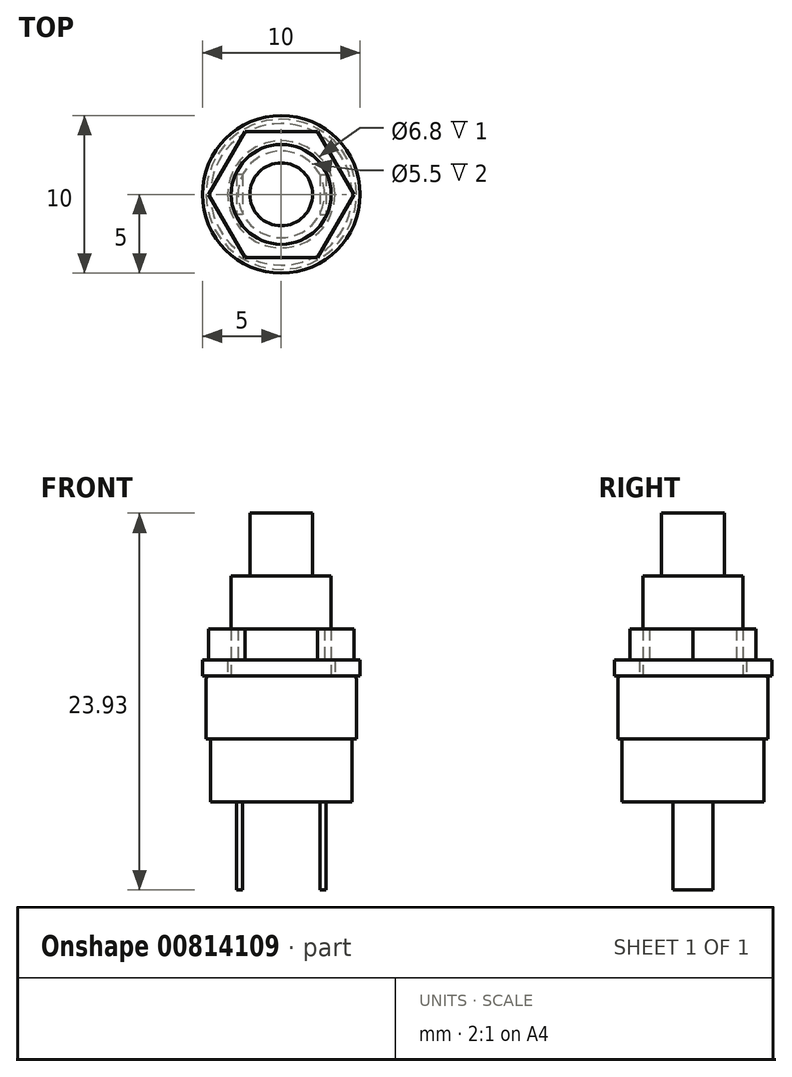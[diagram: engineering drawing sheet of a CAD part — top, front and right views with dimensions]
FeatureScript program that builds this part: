
annotation { "Feature Type Name" : "Feature", "Feature Type Description" : "" }
export const myFeature = defineFeature(function(context is Context, id is Id, definition is map)
    precondition{}
    {
        {
            var Q0;
            Q0=qCreatedBy(makeId("Top.planeOp"),FACE);
            var sketch = newSketch(context, id + "F0", { "sketchPlane" : qUnion([Q0])});
            skCircle(sketch, "E0", {"center": v(0, 0) * mm, "radius": 4.77 * mm});
            skCircle(sketch, "E1", {"center": v(0, 0) * mm, "radius": 4.5 * mm});
            skCircle(sketch, "E2", {"center": v(0, 0) * mm, "radius": 3.18 * mm});
            skCircle(sketch, "E3", {"center": v(0, 0) * mm, "radius": 2 * mm});
            skSolve(sketch);
        }
        {
            var Q0;
            Q0=makeQuery(id+"F0.imprint","IMPRINT",FACE,{"disambiguationData":[TD([[makeQuery(id+"F0.imprint","IMPRINT",EDGE,{"derivedFrom":sQuery(id+"F0.wireOp",EDGE,"E3")}),1.0]])]});
            extrude(context, id + "F1", {"entities" : qUnion([Q0]), "depth" : (10.35 + 4) * mm, "offsetDistance" : 25 * mm});
        }
        {
            var Q0;
            Q0=makeQuery(id+"F0.imprint","IMPRINT",FACE,{"disambiguationData":[TD([[makeQuery(id+"F0.imprint","IMPRINT",EDGE,{"derivedFrom":sQuery(id+"F0.wireOp",EDGE,"E3")}),1.0]])]});
            var Q1;
            Q1=makeQuery(id+"F0.imprint","IMPRINT",FACE,{"disambiguationData":[TD([[makeQuery(id+"F0.imprint","IMPRINT",EDGE,{"derivedFrom":sQuery(id+"F0.wireOp",EDGE,"E2")}),1.0]])]});
            extrude(context, id + "F2", {"entities" : qUnion([Q0, Q1]), "depth" : 10.35 * mm, "offsetDistance" : 25 * mm});
        }
        {
            var Q0;
            Q0=makeQuery(id+"F0.imprint","IMPRINT",FACE,{"disambiguationData":[TD([[makeQuery(id+"F0.imprint","IMPRINT",EDGE,{"derivedFrom":sQuery(id+"F0.wireOp",EDGE,"E0")}),1.0]])]});
            var Q1;
            Q1=makeQuery(id+"F0.imprint","IMPRINT",FACE,{"disambiguationData":[TD([[makeQuery(id+"F0.imprint","IMPRINT",EDGE,{"derivedFrom":sQuery(id+"F0.wireOp",EDGE,"E1")}),1.0]])]});
            var Q2;
            Q2=makeQuery(id+"F0.imprint","IMPRINT",FACE,{"disambiguationData":[TD([[makeQuery(id+"F0.imprint","IMPRINT",EDGE,{"derivedFrom":sQuery(id+"F0.wireOp",EDGE,"E2")}),1.0]])]});
            var Q3;
            Q3=makeQuery(id+"F0.imprint","IMPRINT",FACE,{"disambiguationData":[TD([[makeQuery(id+"F0.imprint","IMPRINT",EDGE,{"derivedFrom":sQuery(id+"F0.wireOp",EDGE,"E3")}),1.0]])]});
            extrude(context, id + "F3", {"entities" : qUnion([Q0, Q1, Q2, Q3]), "operationType" : NewBodyOperationType.ADD, "depth" : 4 * mm, "offsetDistance" : 25 * mm});
        }
        {
            var Q0;
            Q0=makeQuery(id+"F0.imprint","IMPRINT",FACE,{"disambiguationData":[TD([[makeQuery(id+"F0.imprint","IMPRINT",EDGE,{"derivedFrom":sQuery(id+"F0.wireOp",EDGE,"E3")}),1.0]])]});
            var Q1;
            Q1=makeQuery(id+"F0.imprint","IMPRINT",FACE,{"disambiguationData":[TD([[makeQuery(id+"F0.imprint","IMPRINT",EDGE,{"derivedFrom":sQuery(id+"F0.wireOp",EDGE,"E2")}),1.0]])]});
            var Q2;
            Q2=makeQuery(id+"F0.imprint","IMPRINT",FACE,{"disambiguationData":[TD([[makeQuery(id+"F0.imprint","IMPRINT",EDGE,{"derivedFrom":sQuery(id+"F0.wireOp",EDGE,"E1")}),1.0]])]});
            extrude(context, id + "F4", {"entities" : qUnion([Q0, Q1, Q2]), "operationType" : NewBodyOperationType.ADD, "oppositeDirection" : true, "depth" : 4 * mm, "offsetDistance" : 25 * mm});
        }
        {
            var Q0;
            Q0=makeQuery(id+"F4.opExtrude","CAP_FACE",FACE,{"disambiguationData":[OSD([sQuery(id+"F0.wireOp",EDGE,"E1")])],"isStart":false});
            var sketch = newSketch(context, id + "F5", { "sketchPlane" : qUnion([Q0])});
            skLineSegment(sketch, "E4", {"start": v(0, 5.46) * mm, "end": v(0, -5.9) * mm, "construction": true});
            skLineSegment(sketch, "E5", {"start": v(6.94, 0) * mm, "end": v(-5.97, 0) * mm, "construction": true});
            skLineSegment(sketch, "E6.bottom", {"start": v(-2.47, -1.27) * mm, "end": v(-2.85, -1.27) * mm});
            skLineSegment(sketch, "E6.top", {"start": v(-2.47, 1.27) * mm, "end": v(-2.85, 1.27) * mm});
            skLineSegment(sketch, "E6.left", {"start": v(-2.47, -1.27) * mm, "end": v(-2.47, 1.27) * mm});
            skLineSegment(sketch, "E6.right", {"start": v(-2.85, -1.27) * mm, "end": v(-2.85, 1.27) * mm});
            skPoint(sketch, "E6.middle", {"position": v(-2.65, 0) * mm});
            skLineSegment(sketch, "E7.MirrorCS", {"start": v(2.47, -1.27) * mm, "end": v(2.85, -1.27) * mm});
            skLineSegment(sketch, "E8.MirrorCS", {"start": v(2.47, 1.27) * mm, "end": v(2.85, 1.27) * mm});
            skPoint(sketch, "E9.MirrorP", {"position": v(2.65, 0) * mm});
            skLineSegment(sketch, "E10.MirrorCS", {"start": v(2.85, -1.27) * mm, "end": v(2.85, 1.27) * mm});
            skLineSegment(sketch, "E11.MirrorCS", {"start": v(2.47, -1.27) * mm, "end": v(2.47, 1.27) * mm});
            skSolve(sketch);
        }
        {
            var Q0;
            Q0 = qSketchRegion(id + "F5", true);
            extrude(context, id + "F6", {"entities" : qUnion([Q0]), "operationType" : NewBodyOperationType.ADD, "depth" : 5.6 * mm, "offsetDistance" : 25 * mm});
        }
        {
            var Q0;
            Q0=makeQuery(id+"F3.opExtrude","CAP_EDGE",EDGE,{"disambiguationData":[OSD([sQuery(id+"F0.wireOp",EDGE,"E0")])],"isStart":false});
            fillet(context, id + "F7", {"entities" : qUnion([Q0]), "radius" : 0.2 * mm, "tangentPropagation" : true, "allowEdgeOverflow" : false});
        }
        {
            var Q0;
            Q0=makeQuery(id+"F3.opExtrude","CAP_FACE",FACE,{"disambiguationData":[OSD([sQuery(id+"F0.wireOp",EDGE,"E0")])],"isStart":false});
            var sketch = newSketch(context, id + "F8", { "sketchPlane" : qUnion([Q0])});
            skCircle(sketch, "E12", {"center": v(0, 0) * mm, "radius": 3.4 * mm});
            skCircle(sketch, "E13", {"center": v(0, 0) * mm, "radius": 5 * mm});
            skSolve(sketch);
        }
        {
            var Q0;
            Q0 = qSketchRegion(id + "F8", true);
            extrude(context, id + "F9", {"entities" : qUnion([Q0]), "depth" : 1 * mm, "offsetDistance" : 25 * mm});
        }
        {
            var Q0;
            Q0=makeQuery(id+"F9.opExtrude","CAP_FACE",FACE,{"disambiguationData":[OSD([sQuery(id+"F8.wireOp",EDGE,"E12"),sQuery(id+"F8.wireOp",EDGE,"E13")])],"isStart":false});
            var sketch = newSketch(context, id + "F10", { "sketchPlane" : qUnion([Q0])});
            skCircle(sketch, "E14", {"center": v(0, 0) * mm, "radius": 4 * mm, "construction": true});
            skLineSegment(sketch, "E15", {"start": v(-2.3, 4) * mm, "end": v(2.3, 4) * mm});
            skLineSegment(sketch, "E16", {"start": v(2.3, 4) * mm, "end": v(4.62, 0) * mm});
            skLineSegment(sketch, "E17", {"start": v(4.62, 0) * mm, "end": v(2.3, -4) * mm});
            skLineSegment(sketch, "E18", {"start": v(2.3, -4) * mm, "end": v(-2.3, -4) * mm});
            skLineSegment(sketch, "E19", {"start": v(-2.3, -4) * mm, "end": v(-4.62, 0) * mm});
            skLineSegment(sketch, "E20", {"start": v(-4.62, 0) * mm, "end": v(-2.3, 4) * mm});
            skCircle(sketch, "E21", {"center": v(0, 0) * mm, "radius": 2.75 * mm});
            skSolve(sketch);
        }
        {
            var Q0;
            Q0 = qSketchRegion(id + "F10", true);
            extrude(context, id + "F11", {"entities" : qUnion([Q0]), "depth" : 2 * mm, "offsetDistance" : 25 * mm});
        }
    });
